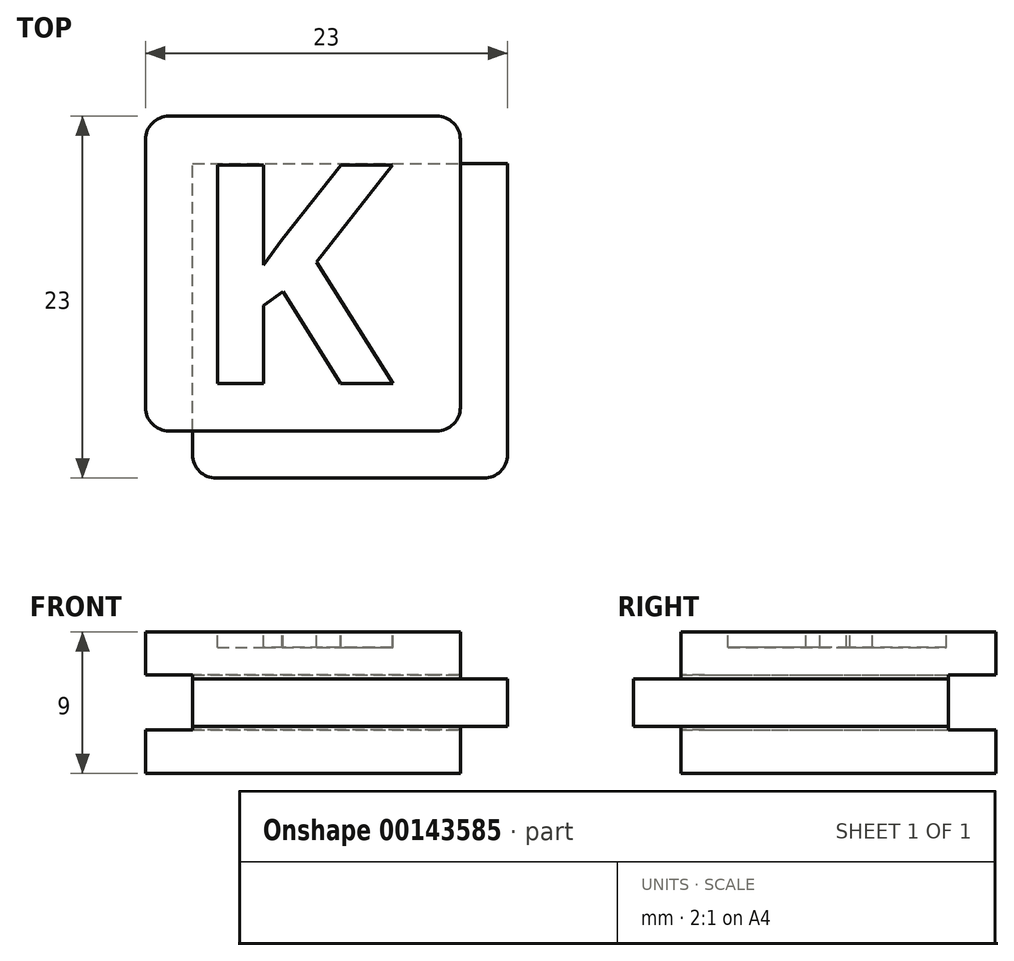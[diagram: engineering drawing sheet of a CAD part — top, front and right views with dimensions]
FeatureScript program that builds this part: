
annotation { "Feature Type Name" : "Feature", "Feature Type Description" : "" }
export const myFeature = defineFeature(function(context is Context, id is Id, definition is map)
    precondition{}
    {
        {
            var Q0;
            Q0=qCreatedBy(makeId("Front.planeOp"),FACE);
            var sketch = newSketch(context, id + "F0", { "sketchPlane" : qUnion([Q0])});
            skLineSegment(sketch, "E0.bottom", {"start": v(10, 4.5) * mm, "end": v(-10, 4.5) * mm});
            skLineSegment(sketch, "E0.top", {"start": v(10, -4.5) * mm, "end": v(-10, -4.5) * mm});
            skLineSegment(sketch, "E0.left", {"start": v(10, 4.5) * mm, "end": v(10, -4.5) * mm});
            skLineSegment(sketch, "E0.right", {"start": v(-10, 4.5) * mm, "end": v(-10, -4.5) * mm});
            skPoint(sketch, "E0.middle", {"position": v(0, 0) * mm});
            skLineSegment(sketch, "E1.bottom", {"start": v(13, 1.5) * mm, "end": v(7, 1.5) * mm});
            skLineSegment(sketch, "E1.top", {"start": v(13, -1.5) * mm, "end": v(7, -1.5) * mm});
            skLineSegment(sketch, "E1.left", {"start": v(13, 1.5) * mm, "end": v(13, -1.5) * mm});
            skLineSegment(sketch, "E1.right", {"start": v(7, 1.5) * mm, "end": v(7, -1.5) * mm});
            skPoint(sketch, "E1.middle", {"position": v(10, 0) * mm});
            skLineSegment(sketch, "E2.bottom", {"start": v(7, 1.5) * mm, "end": v(-7, 1.5) * mm});
            skLineSegment(sketch, "E2.top", {"start": v(7, -1.5) * mm, "end": v(-7, -1.5) * mm});
            skLineSegment(sketch, "E2.right", {"start": v(-7, 1.5) * mm, "end": v(-7, -1.5) * mm});
            skLineSegment(sketch, "E3.bottom", {"start": v(-7, -1.5) * mm, "end": v(-10, -1.5) * mm});
            skLineSegment(sketch, "E3.top", {"start": v(-7, 1.5) * mm, "end": v(-10, 1.5) * mm});
            skLineSegment(sketch, "E3.left", {"start": v(-7, -1.5) * mm, "end": v(-7, 1.5) * mm});
            skLineSegment(sketch, "E3.right", {"start": v(-10, -1.5) * mm, "end": v(-10, 1.5) * mm});
            skSolve(sketch);
        }
        {
            var Q0;
            {var subQ5=sQuery(id+"F0.wireOp",EDGE,"E0.bottom");Q0=makeQuery(id+"F0.imprint","IMPRINT",FACE,{"disambiguationData":[TD([[makeQuery(id+"F0.imprint","IMPRINT",EDGE,{"derivedFrom":subQ5}),1.0]])]});}
            var Q1;
            Q1=makeQuery(id+"F0.imprint","IMPRINT",FACE,{"disambiguationData":[TD([[makeQuery(id+"F0.imprint","IMPRINT",EDGE,{"derivedFrom":sQuery(id+"F0.wireOp",EDGE,"E2.bottom")}),1.0]])]});
            var Q2;
            {var subQ5=sQuery(id+"F0.wireOp",EDGE,"E1.left");Q2=makeQuery(id+"F0.imprint","IMPRINT",FACE,{"disambiguationData":[TD([[makeQuery(id+"F0.imprint","IMPRINT",EDGE,{"derivedFrom":subQ5}),-1.0]])]});}
            var Q3;
            {var subQ5=sQuery(id+"F0.wireOp",EDGE,"E1.right");Q3=makeQuery(id+"F0.imprint","IMPRINT",FACE,{"disambiguationData":[TD([[makeQuery(id+"F0.imprint","IMPRINT",EDGE,{"derivedFrom":subQ5}),1.0]])]});}
            var Q4;
            Q4=makeQuery(id+"F0.imprint","IMPRINT",FACE,{"disambiguationData":[TD([[makeQuery(id+"F0.imprint","IMPRINT",EDGE,{"derivedFrom":sQuery(id+"F0.wireOp",EDGE,"E3.bottom")}),-1.0]])]});
            var Q5;
            {var subQ5=sQuery(id+"F0.wireOp",EDGE,"E0.top");Q5=makeQuery(id+"F0.imprint","IMPRINT",FACE,{"disambiguationData":[TD([[makeQuery(id+"F0.imprint","IMPRINT",EDGE,{"derivedFrom":subQ5}),-1.0]])]});}
            extrude(context, id + "F1", {"entities" : qUnion([Q0, Q1, Q2, Q3, Q4, Q5]), "oppositeDirection" : true, "depth" : 20 * mm});
        }
        {
            var Q0;
            Q0=makeQuery(id+"F0.imprint","IMPRINT",FACE,{"disambiguationData":[TD([[makeQuery(id+"F0.imprint","IMPRINT",EDGE,{"derivedFrom":sQuery(id+"F0.wireOp",EDGE,"E3.bottom")}),-1.0]])]});
            var Q1;
            Q1=makeQuery(id+"F0.imprint","IMPRINT",FACE,{"disambiguationData":[TD([[makeQuery(id+"F0.imprint","IMPRINT",EDGE,{"derivedFrom":sQuery(id+"F0.wireOp",EDGE,"E2.bottom")}),1.0]])]});
            var Q2;
            {var subQ5=sQuery(id+"F0.wireOp",EDGE,"E1.right");Q2=makeQuery(id+"F0.imprint","IMPRINT",FACE,{"disambiguationData":[TD([[makeQuery(id+"F0.imprint","IMPRINT",EDGE,{"derivedFrom":subQ5}),1.0]])]});}
            var Q3;
            {var subQ5=sQuery(id+"F0.wireOp",EDGE,"E1.left");Q3=makeQuery(id+"F0.imprint","IMPRINT",FACE,{"disambiguationData":[TD([[makeQuery(id+"F0.imprint","IMPRINT",EDGE,{"derivedFrom":subQ5}),-1.0]])]});}
            extrude(context, id + "F2", {"entities" : qUnion([Q0, Q1, Q2, Q3]), "operationType" : NewBodyOperationType.ADD, "depth" : 3 * mm});
        }
        {
            var Q0;
            {var subQ0=sQuery(id+"F0.wireOp",EDGE,"E1.left");Q0=makeQuery(id+"F2.boolean.opBoolean","MERGE",FACE,{"derivedFrom":[makeQuery(id+"F1.opExtrude","SWEPT_FACE",FACE,{"disambiguationData":[OSD([subQ0])]}),makeQuery(id+"F2.opExtrude","SWEPT_FACE",FACE,{"disambiguationData":[OSD([subQ0])]})]});}
            var sketch = newSketch(context, id + "F3", { "sketchPlane" : qUnion([Q0])});
            skLineSegment(sketch, "E4.bottom", {"start": v(23, 1.75) * mm, "end": v(17, 1.75) * mm});
            skLineSegment(sketch, "E4.top", {"start": v(23, -1.75) * mm, "end": v(17, -1.75) * mm});
            skLineSegment(sketch, "E4.left", {"start": v(23, 1.75) * mm, "end": v(23, -1.75) * mm});
            skLineSegment(sketch, "E4.right", {"start": v(17, 1.75) * mm, "end": v(17, -1.75) * mm});
            skPoint(sketch, "E4.middle", {"position": v(20, 0) * mm});
            skSolve(sketch);
        }
        {
            var Q0;
            {var subQ1=sQuery(id+"F3.wireOp",EDGE,"E4.bottom");Q0=makeQuery(id+"F3.imprint","IMPRINT",FACE,{"disambiguationData":[TD([[makeQuery(id+"F3.imprint","IMPRINT",EDGE,{"derivedFrom":subQ1}),1.0]])]});}
            var Q1;
            {var subQ1=sQuery(id+"F0.wireOp",EDGE,"E1.left");var subQ8=makeQuery(id+"F1.opExtrude","CAP_EDGE",EDGE,{"disambiguationData":[OSD([subQ1])],"isStart":false});Q1=makeQuery(id+"F3.imprint","IMPRINT",FACE,{"disambiguationData":[TD([[makeQuery(id+"F3.imprint","IMPRINT",EDGE,{"derivedFrom":subQ8}),-1.0]])]});}
            extrude(context, id + "F4", {"entities" : qUnion([Q0, Q1]), "operationType" : NewBodyOperationType.REMOVE, "oppositeDirection" : true, "depth" : 100 * mm});
        }
        {
            var Q0;
            Q0=makeQuery(id+"F4.boolean.opBoolean","COPY",FACE,{"derivedFrom":makeQuery(id+"F4.opExtrude","SWEPT_FACE",FACE,{"disambiguationData":[OSD([sQuery(id+"F3.wireOp",EDGE,"E4.right")])]})});
            var sketch = newSketch(context, id + "F5", { "sketchPlane" : qUnion([Q0])});
            skLineSegment(sketch, "E5.bottom", {"start": v(13, 1.75) * mm, "end": v(7, 1.75) * mm});
            skLineSegment(sketch, "E5.top", {"start": v(13, -1.75) * mm, "end": v(7, -1.75) * mm});
            skLineSegment(sketch, "E5.left", {"start": v(13, 1.75) * mm, "end": v(13, -1.75) * mm});
            skLineSegment(sketch, "E5.right", {"start": v(7, 1.75) * mm, "end": v(7, -1.75) * mm});
            skPoint(sketch, "E5.middle", {"position": v(10, 0) * mm});
            skSolve(sketch);
        }
        {
            var Q0;
            {var subQ3=sQuery(id+"F5.wireOp",EDGE,"E5.left");Q0=makeQuery(id+"F5.imprint","IMPRINT",FACE,{"disambiguationData":[TD([[makeQuery(id+"F5.imprint","IMPRINT",EDGE,{"derivedFrom":subQ3}),-1.0]])]});}
            var Q1;
            {var subQ4=sQuery(id+"F5.wireOp",EDGE,"E5.right");Q1=makeQuery(id+"F5.imprint","IMPRINT",FACE,{"disambiguationData":[TD([[makeQuery(id+"F5.imprint","IMPRINT",EDGE,{"derivedFrom":subQ4}),1.0]])]});}
            extrude(context, id + "F6", {"entities" : qUnion([Q0, Q1]), "operationType" : NewBodyOperationType.REMOVE, "oppositeDirection" : true, "depth" : 100 * mm});
        }
        {
            var Q0;
            Q0=makeQuery(id+"F6.boolean.opBoolean","INTERSECT",EDGE,{"derivedFrom":[makeQuery(id+"F2.opExtrude","CAP_FACE",FACE,{"disambiguationData":[OSD([sQuery(id+"F0.wireOp",EDGE,"E1.bottom"),sQuery(id+"F0.wireOp",EDGE,"E1.top"),sQuery(id+"F0.wireOp",EDGE,"E1.left"),sQuery(id+"F0.wireOp",EDGE,"E2.bottom"),sQuery(id+"F0.wireOp",EDGE,"E2.top"),sQuery(id+"F0.wireOp",EDGE,"E3.bottom"),sQuery(id+"F0.wireOp",EDGE,"E3.top"),sQuery(id+"F0.wireOp",EDGE,"E3.right")])],"isStart":false}),makeQuery(id+"F6.opExtrude","SWEPT_FACE",FACE,{"disambiguationData":[OSD([sQuery(id+"F5.wireOp",EDGE,"E5.right")])]})]});
            var Q1;
            Q1=makeQuery(id+"F2.opExtrude","CAP_EDGE",EDGE,{"disambiguationData":[OSD([sQuery(id+"F0.wireOp",EDGE,"E1.left")])],"isStart":false});
            var Q2;
            {var subQ0=sQuery(id+"F0.wireOp",EDGE,"E0.left");Q2=makeQuery(id+"F1.opExtrude","CAP_EDGE",EDGE,{"disambiguationData":[OSD([subQ0]),TDD([makeQuery(id+"F0.imprint","IMPRINT",EDGE,{"disambiguationData":[TD([[makeQuery(id+"F0.imprint","INTERSECT",VERTEX,{"derivedFrom":[sQuery(id+"F0.wireOp",EDGE,"E0.bottom"),subQ0]}),-1.0]])],"derivedFrom":subQ0})])],"isStart":true});}
            var Q3;
            {var subQ0=sQuery(id+"F0.wireOp",EDGE,"E0.left");Q3=makeQuery(id+"F1.opExtrude","CAP_EDGE",EDGE,{"disambiguationData":[OSD([subQ0]),TDD([makeQuery(id+"F0.imprint","IMPRINT",EDGE,{"disambiguationData":[TD([[makeQuery(id+"F0.imprint","INTERSECT",VERTEX,{"derivedFrom":[sQuery(id+"F0.wireOp",EDGE,"E0.top"),subQ0]}),1.0]])],"derivedFrom":subQ0})])],"isStart":true});}
            var Q4;
            {var subQ0=sQuery(id+"F0.wireOp",EDGE,"E3.right");var subQ1=sQuery(id+"F0.wireOp",EDGE,"E0.right");var subQ3=sQuery(id+"F0.wireOp",EDGE,"E0.top");Q4=makeQuery(id+"F2.boolean.opBoolean","SPLIT",EDGE,{"disambiguationData":[TD([makeQuery(id+"F1.opExtrude","SWEPT_FACE",FACE,{"disambiguationData":[OSD([subQ3])]})])],"derivedFrom":makeQuery(id+"F1.opExtrude","CAP_EDGE",EDGE,{"disambiguationData":[OSD([subQ1,subQ0])],"isStart":true})});}
            var Q5;
            {var subQ1=sQuery(id+"F0.wireOp",EDGE,"E3.right");var subQ2=sQuery(id+"F0.wireOp",EDGE,"E0.right");var subQ3=sQuery(id+"F0.wireOp",EDGE,"E0.bottom");Q5=makeQuery(id+"F2.boolean.opBoolean","SPLIT",EDGE,{"disambiguationData":[TD([makeQuery(id+"F1.opExtrude","SWEPT_FACE",FACE,{"disambiguationData":[OSD([subQ3])]})])],"derivedFrom":makeQuery(id+"F1.opExtrude","CAP_EDGE",EDGE,{"disambiguationData":[OSD([subQ2,subQ1])],"isStart":true})});}
            var Q6;
            Q6=makeQuery(id+"F6.boolean.opBoolean","COPY",EDGE,{"derivedFrom":makeQuery(id+"F6.opExtrude","CAP_EDGE",EDGE,{"disambiguationData":[OSD([sQuery(id+"F5.wireOp",EDGE,"E5.right")])],"isStart":true})});
            var Q7;
            {var subQ0=sQuery(id+"F0.wireOp",EDGE,"E3.right");var subQ1=sQuery(id+"F0.wireOp",EDGE,"E0.right");var subQ2=sQuery(id+"F0.wireOp",EDGE,"E0.bottom");Q7=makeQuery(id+"F4.boolean.opBoolean","SPLIT",EDGE,{"disambiguationData":[TD([makeQuery(id+"F1.opExtrude","SWEPT_FACE",FACE,{"disambiguationData":[OSD([subQ2])]})])],"derivedFrom":makeQuery(id+"F1.opExtrude","CAP_EDGE",EDGE,{"disambiguationData":[OSD([subQ1,subQ0])],"isStart":false})});}
            var Q8;
            {var subQ0=sQuery(id+"F0.wireOp",EDGE,"E3.right");var subQ1=sQuery(id+"F0.wireOp",EDGE,"E0.right");var subQ2=sQuery(id+"F0.wireOp",EDGE,"E0.top");Q8=makeQuery(id+"F4.boolean.opBoolean","SPLIT",EDGE,{"disambiguationData":[TD([makeQuery(id+"F1.opExtrude","SWEPT_FACE",FACE,{"disambiguationData":[OSD([subQ2])]})])],"derivedFrom":makeQuery(id+"F1.opExtrude","CAP_EDGE",EDGE,{"disambiguationData":[OSD([subQ1,subQ0])],"isStart":false})});}
            var Q9;
            Q9=makeQuery(id+"F4.boolean.opBoolean","COPY",EDGE,{"derivedFrom":makeQuery(id+"F4.opExtrude","CAP_EDGE",EDGE,{"disambiguationData":[OSD([sQuery(id+"F3.wireOp",EDGE,"E4.right")])],"isStart":true})});
            var Q10;
            {var subQ0=sQuery(id+"F0.wireOp",EDGE,"E0.left");Q10=makeQuery(id+"F1.opExtrude","CAP_EDGE",EDGE,{"disambiguationData":[OSD([subQ0]),TDD([makeQuery(id+"F0.imprint","IMPRINT",EDGE,{"disambiguationData":[TD([[makeQuery(id+"F0.imprint","INTERSECT",VERTEX,{"derivedFrom":[sQuery(id+"F0.wireOp",EDGE,"E0.bottom"),subQ0]}),-1.0]])],"derivedFrom":subQ0})])],"isStart":false});}
            var Q11;
            {var subQ0=sQuery(id+"F0.wireOp",EDGE,"E0.left");Q11=makeQuery(id+"F1.opExtrude","CAP_EDGE",EDGE,{"disambiguationData":[OSD([subQ0]),TDD([makeQuery(id+"F0.imprint","IMPRINT",EDGE,{"disambiguationData":[TD([[makeQuery(id+"F0.imprint","INTERSECT",VERTEX,{"derivedFrom":[sQuery(id+"F0.wireOp",EDGE,"E0.top"),subQ0]}),1.0]])],"derivedFrom":subQ0})])],"isStart":false});}
            fillet(context, id + "F7", {"entities" : qUnion([Q0, Q1, Q2, Q3, Q4, Q5, Q6, Q7, Q8, Q9, Q10, Q11]), "radius" : 1.5 * mm, "tangentPropagation" : true, "allowEdgeOverflow" : false});
        }
        {
            var Q0;
            Q0=makeQuery(id+"F1.opExtrude","SWEPT_FACE",FACE,{"disambiguationData":[OSD([sQuery(id+"F0.wireOp",EDGE,"E0.bottom")])]});
            var sketch = newSketch(context, id + "F8", { "sketchPlane" : qUnion([Q0])});
            skText(sketch, "E6", { "text": "K", "fontName": "OpenSans-Bold.ttf"});
            skLineSegment(sketch, "E7.0", {"start": v(10.88, 3) * mm, "end": v(-11.07, 3) * mm});
            const initialGuessF8  = {"E6": [-0.00718, 0.003, 1, 0, 0.014]};
            skSetInitialGuess(sketch, initialGuessF8);
            skSolve(sketch);
        }
        {
            var Q0;
            {var subQ0=sQuery(id+"F8.wireOp",EDGE,"E6.sketch_text.stroke-1");Q0=makeQuery(id+"F8.imprint","IMPRINT",FACE,{"disambiguationData":[TD([[makeQuery(id+"F8.imprint","IMPRINT",EDGE,{"derivedFrom":subQ0}),-1.0]])]});}
            extrude(context, id + "F9", {"entities" : qUnion([Q0]), "operationType" : NewBodyOperationType.REMOVE, "oppositeDirection" : true, "depth" : 1 * mm});
        }
    });
